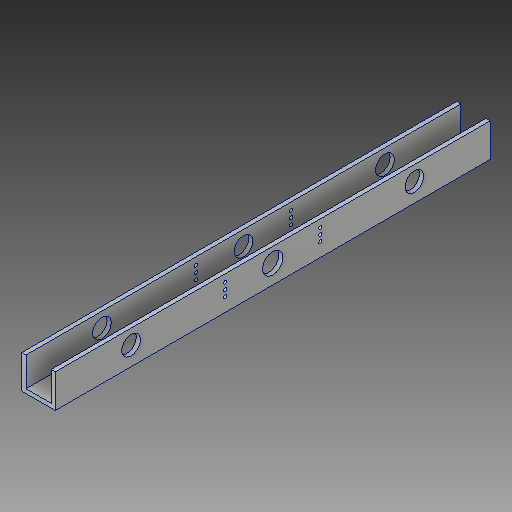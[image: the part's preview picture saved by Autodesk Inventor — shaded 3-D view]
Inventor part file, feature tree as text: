
AUTODESK INVENTOR PART (.ipt)
format: ipt  version: 2018 (Build 220112000, 112)  size: 159,744 bytes
history: native  units: in
note: dims shown in document units (in); Inventor stores cm internally (conversion verified against a paired STEP export)
features: extrude x4, sketch x4
ambient origin geometry x8: Origin, YZ Plane, XZ Plane, XY Plane, X Axis, Y Axis, Z Axis, Center Point
bodies: Solid1 (feature_tree)
feature tree (8):
  extrude  "Extrusion1"  Depth=2.0in
  extrude  "Extrusion2"  Depth=0.25in
  extrude  "Extrusion3"  Depth=26.0in TaperAngle=0.0deg
  extrude  "Extrusion4"  Depth=26.0in
  sketch  "Sketch1"  dims[d0=0.25in d1=2.0in]
  sketch  "Sketch2"  dims[d2=2.0in d3=0.25in]
  sketch  "Sketch3"  dims[d4=0.25in d5=26.0in d6=0.0in]
  sketch  "Sketch4"  dims[d7=0.25in d8=4.535in d9=1.125in d10=4.535in d11=1.125in d12=26.0in d13=0.0in d14=1.225in d15=1.0in d16=0.0in d17=2.845in d18=0.438in d19=0.375in d20=0.375in d21=2.845in d22=0.2in d23=3.3125in d24=0.0in]
